# Revit family: LAMP_HANCE TRACK FLOOD (DALI)
name_source: partatom
category: Modelos genéricos
revit_build: Autodesk Revit 2015 (Build: 20140606_1530(x64)
units: mm (PartAtom-declared; Revit-internal decimal feet)

## types (16) — shared parameters
CRI = 80
Comentarios de tipo = Availability of tilting between 0º and 90º, rotation between 0º and 355º and change ring color when placed in a project.
Elevación por defecto = 1219 mm
Fabricante = LAMP
Gear = Adjustable DALI
Installation instructions = http://www.lamp.es
Insulation class = I
Lamp = COB LED
Last update = 08/08/2018
Luminaire type = Indoor - Spotlight
MacAdam = 3
Manufacturer URL = http://www.lamp.es
Manufacturer country = Spain
Manufacturer name = LAMP
Model explanation = Availability of tilting between 0º and 90º, rotation between 0º and 355º and change ring color when placed in a project.
Power Supply = 220-240V 50-60Hz
Product URL = http://www.lamp.es
Product datasheet = http://www.lamp.es
Protection rating = IP20
Type = COB PHILIPS

## per-type parameters (varying)
| type | Altura tija | Anchura tija | Body height | Descripción | Diameter | Efficacy | Finish | IEE | Initial color | Initial intensity | LED Lifetime | Longitud aro | Longitud cuerpo | Material tija | Material track | Modelo | Photometric web file | Plum | Power | Product code | Profundidad tija | Total height | Weight |
| 639LM 3000 BLACK | 63 mm  [stored 0.206693 ft] | 23 mm  [stored 0.0754593 ft] | 135 mm  [stored 0.442913 ft] | HANCE TRACK 220 1000 WW FL BK. | 65 mm  [stored 0.213255 ft] | 78 lm/W | Texturised black | A+ | 3000 K | 639 lm | 50.000 L90 B10 | 64 mm | 135 mm  [stored 0.442913 ft] | LAMP_Aluminio Hance Negro | LAMP_Aluminio Hance Negro | HS1TK10FL830DBB | Cuerpo Hance TRACK FLOOD (tilting) : 639LM 3000 BLACK | 8 W | 7 W | HS1TK10FL830DBB | 8 mm  [stored 0.0262467 ft] | 190 mm | 0.47 kg |
| 639LM 3000 WHITE | 63 mm  [stored 0.206693 ft] | 23 mm  [stored 0.0754593 ft] | 135 mm  [stored 0.442913 ft] | HANCE TRACK 220 1000 WW FL WH. | 65 mm  [stored 0.213255 ft] | 78 lm/W | Texturised matt white | A+ | 3000 K | 639 lm | 50.000 L90 B10 | 64 mm | 135 mm  [stored 0.442913 ft] | LAMP_Aluminio Hance Blanco | LAMP_Aluminio Hance Blanco | HS1TK10FL830DBW | Cuerpo Hance TRACK FLOOD (tilting) : 639LM 3000 WHITE | 8 W | 7 W | HS1TK10FL830DBW | 8 mm  [stored 0.0262467 ft] | 190 mm | 0.47 kg |
| 675LM 4000 BLACK | 63 mm  [stored 0.206693 ft] | 23 mm  [stored 0.0754593 ft] | 135 mm  [stored 0.442913 ft] | HANCE TRACK 220 1000 NW FL BK. | 65 mm  [stored 0.213255 ft] | 82 lm/W | Texturised black | A+ | 4000 K | 675 lm | 50.000 L90 B10 | 64 mm | 135 mm  [stored 0.442913 ft] | LAMP_Aluminio Hance Negro | LAMP_Aluminio Hance Negro | HS1TK10FL840DBB | Cuerpo Hance TRACK FLOOD (tilting) : 675LM 4000 BLACK | 8 W | 7 W | HS1TK10FL840DBB | 8 mm  [stored 0.0262467 ft] | 190 mm | 0.47 kg |
| 675LM 4000 WHITE | 63 mm  [stored 0.206693 ft] | 23 mm  [stored 0.0754593 ft] | 135 mm  [stored 0.442913 ft] | HANCE TRACK 220 1000 NW FL WH. | 65 mm  [stored 0.213255 ft] | 82 lm/W | Texturised matt white | A+ | 4000 K | 675 lm | 50.000 L90 B10 | 64 mm | 135 mm  [stored 0.442913 ft] | LAMP_Aluminio Hance Blanco | LAMP_Aluminio Hance Blanco | HS1TK10FL840DBW | Cuerpo Hance TRACK FLOOD (tilting) : 675LM 4000 WHITE | 8 W | 7 W | HS1TK10FL840DBW | 8 mm  [stored 0.0262467 ft] | 190 mm | 0.47 kg |
| 1476LM 3000 BLACK | 63 mm  [stored 0.206693 ft] | 23 mm  [stored 0.0754593 ft] | 170 mm  [stored 0.557743 ft] | HANCE TRACK 220 2000 WW FL BK. | 65 mm  [stored 0.213255 ft] | 70 lm/W | Texturised black | A | 3000 K | 1476 lm | 50.000 L80 B10 | 99 mm | 170 mm  [stored 0.557743 ft] | LAMP_Aluminio Hance Negro | LAMP_Aluminio Hance Negro | HS1TK20FL830DBB | Cuerpo Hance TRACK FLOOD (tilting) : 1476LM 3000 BLACK | 21 W | 18 W | HS1TK20FL830DBB | 8 mm  [stored 0.0262467 ft] | 225 mm  [stored 0.738189 ft] | 0.65 kg |
| 1476LM 3000 WHITE | 63 mm  [stored 0.206693 ft] | 23 mm  [stored 0.0754593 ft] | 170 mm  [stored 0.557743 ft] | HANCE TRACK 220 2000 WW FL WH. | 65 mm  [stored 0.213255 ft] | 70 lm/W | Texturised matt white | A | 3000 K | 1476 lm | 50.000 L80 B10 | 99 mm | 170 mm  [stored 0.557743 ft] | LAMP_Aluminio Hance Blanco | LAMP_Aluminio Hance Blanco | HS1TK20FL830DBW | Cuerpo Hance TRACK FLOOD (tilting) : 1476LM 3000 WHITE | 21 W | 18 W | HS1TK20FL830DBW | 8 mm  [stored 0.0262467 ft] | 225 mm  [stored 0.738189 ft] | 0.65 kg |
| 1560LM 4000 BLACK | 63 mm  [stored 0.206693 ft] | 23 mm  [stored 0.0754593 ft] | 170 mm  [stored 0.557743 ft] | HANCE TRACK 220 2000 NW FL BK. | 65 mm  [stored 0.213255 ft] | 74 lm/W | Texturised black | A | 4000 K | 1560 lm | 50.000 L80 B10 | 99 mm | 170 mm  [stored 0.557743 ft] | LAMP_Aluminio Hance Negro | LAMP_Aluminio Hance Negro | HS1TK20FL840DBB
HS1TK20FL840NBB | Cuerpo Hance TRACK FLOOD (tilting) : 1560LM 4000 BLACK | 21 W | 18 W | HS1TK20FL840DBB
HS1TK20FL840NBB | 8 mm  [stored 0.0262467 ft] | 225 mm  [stored 0.738189 ft] | 0.65 kg |
| 1560LM 4000 WHITE | 63 mm  [stored 0.206693 ft] | 23 mm  [stored 0.0754593 ft] | 170 mm  [stored 0.557743 ft] | HANCE TRACK 220 2000 NW FL WH. | 65 mm  [stored 0.213255 ft] | 74 lm/W | Texturised matt white | A | 4000 K | 1560 lm | 50.000 L80 B10 | 99 mm | 170 mm  [stored 0.557743 ft] | LAMP_Aluminio Hance Blanco | LAMP_Aluminio Hance Blanco | HS1TK20FL840DBW
HS1TK20FL840NBB | Cuerpo Hance TRACK FLOOD (tilting) : 1560LM 4000 WHITE | 21 W | 18 W | HS1TK20FL840DBW
HS1TK20FL840NBB | 8 mm  [stored 0.0262467 ft] | 225 mm  [stored 0.738189 ft] | 0.65 kg |
| 2569LM 3000 BLACK | 49 mm  [stored 0.160761 ft] | 28 mm  [stored 0.0918635 ft] | 210 mm  [stored 0.688976 ft] | HANCE TRACK 220 3000 WW FL BK. | 90 mm  [stored 0.295276 ft] | 90 lm/W | Texturised black | A+ | 3000 K | 2569 lm | 50.000 L80 B10 | 139 mm | 210 mm  [stored 0.688976 ft] | LAMP_Aluminio Hance Negro | LAMP_Aluminio Hance Negro | HS1TK30FL830DBB | Cuerpo Hance TRACK FLOOD (tilting) : 2569LM 3000 BLACK | 29 W | 26 W | HS1TK30FL830DBB | 18 mm  [stored 0.0590551 ft] | 266 mm  [stored 0.872703 ft] | 1.35 kg |
| 2569LM 3000 WHITE | 49 mm  [stored 0.160761 ft] | 28 mm  [stored 0.0918635 ft] | 210 mm  [stored 0.688976 ft] | HANCE TRACK 220 3000 WW FL WH. | 90 mm  [stored 0.295276 ft] | 90 lm/W | Texturised matt white | A+ | 3000 K | 2569 lm | 50.000 L80 B10 | 139 mm | 210 mm  [stored 0.688976 ft] | LAMP_Aluminio Hance Blanco | LAMP_Aluminio Hance Blanco | HS1TK30FL830DBW | Cuerpo Hance TRACK FLOOD (tilting) : 2569LM 3000 WHITE | 29 W | 26 W | HS1TK30FL830DBW | 18 mm  [stored 0.0590551 ft] | 266 mm  [stored 0.872703 ft] | 1.35 kg |
| 2686LM 4000 BLACK | 49 mm  [stored 0.160761 ft] | 28 mm  [stored 0.0918635 ft] | 210 mm  [stored 0.688976 ft] | HANCE TRACK 220 3000 NW FL BK. | 90 mm  [stored 0.295276 ft] | 94 lm/W | Texturised black | A+ | 4000 K | 2686 lm | 50.000 L80 B10 | 139 mm | 210 mm  [stored 0.688976 ft] | LAMP_Aluminio Hance Negro | LAMP_Aluminio Hance Negro | HS1TK30FL840DBB | Cuerpo Hance TRACK FLOOD (tilting) : 2686LM 4000 BLACK | 29 W | 26 W | HS1TK30FL840DBB | 18 mm  [stored 0.0590551 ft] | 266 mm  [stored 0.872703 ft] | 1.35 kg |
| 2686LM 4000 WHITE | 49 mm  [stored 0.160761 ft] | 28 mm  [stored 0.0918635 ft] | 210 mm  [stored 0.688976 ft] | HANCE TRACK 220 3000 NW FL WH. | 90 mm  [stored 0.295276 ft] | 94 lm/W | Texturised matt white | A+ | 4000 K | 2686 lm | 50.000 L80 B10 | 139 mm | 210 mm  [stored 0.688976 ft] | LAMP_Aluminio Hance Blanco | LAMP_Aluminio Hance Blanco | HS1TK30FL840DBW | Cuerpo Hance TRACK FLOOD (tilting) : 2686LM 4000 WHITE | 29 W | 26 W | HS1TK30FL840DBW | 18 mm  [stored 0.0590551 ft] | 266 mm  [stored 0.872703 ft] | 1.35 kg |
| 3290LM 3000 BLACK | 49 mm  [stored 0.160761 ft] | 28 mm  [stored 0.0918635 ft] | 210 mm  [stored 0.688976 ft] | HANCE TRACK 220 4000 WW FL BK. | 90 mm  [stored 0.295276 ft] | 83 lm/W | Texturised black | A+ | 3000 K | 3290 lm | 50.000 L80 B10 | 139 mm | 210 mm  [stored 0.688976 ft] | LAMP_Aluminio Hance Negro | LAMP_Aluminio Hance Negro | HS1TK40FL830DBB | Cuerpo Hance TRACK FLOOD (tilting) : 3290LM 3000 BLACK | 40 W | 35 W | HS1TK40FL830DBB | 18 mm  [stored 0.0590551 ft] | 266 mm  [stored 0.872703 ft] | 1.35 kg |
| 3290LM 3000 WHITE | 49 mm  [stored 0.160761 ft] | 28 mm  [stored 0.0918635 ft] | 210 mm  [stored 0.688976 ft] | HANCE TRACK 220 4000 WW FL WH. | 90 mm  [stored 0.295276 ft] | 83 lm/W | Texturised matt white | A+ | 3000 K | 3290 lm | 50.000 L80 B10 | 139 mm | 210 mm  [stored 0.688976 ft] | LAMP_Aluminio Hance Blanco | LAMP_Aluminio Hance Blanco | HS1TK40FL830DBW | Cuerpo Hance TRACK FLOOD (tilting) : 3290LM 3000 WHITE | 40 W | 35 W | HS1TK40FL830DBW | 18 mm  [stored 0.0590551 ft] | 266 mm  [stored 0.872703 ft] | 1.35 kg |
| 3426LM 4000 BLACK | 49 mm  [stored 0.160761 ft] | 28 mm  [stored 0.0918635 ft] | 210 mm  [stored 0.688976 ft] | HANCE TRACK 220 4000 NW FL BK. | 90 mm  [stored 0.295276 ft] | 87 lm/W | Texturised black | A+ | 4000 K | 3426 lm | 50.000 L80 B10 | 139 mm | 210 mm  [stored 0.688976 ft] | LAMP_Aluminio Hance Negro | LAMP_Aluminio Hance Negro | HS1TK40FL840DBB | Cuerpo Hance TRACK FLOOD (tilting) : 3426LM 4000 BLACK | 40 W | 35 W | HS1TK40FL840DBB | 18 mm  [stored 0.0590551 ft] | 266 mm  [stored 0.872703 ft] | 1.35 kg |
| 3426LM 4000 WHITE | 49 mm  [stored 0.160761 ft] | 28 mm  [stored 0.0918635 ft] | 210 mm  [stored 0.688976 ft] | HANCE TRACK 220 4000 NW FL WH. | 90 mm  [stored 0.295276 ft] | 87 lm/W | Texturised matt white | A+ | 4000 K | 3426 lm | 50.000 L80 B10 | 139 mm | 210 mm  [stored 0.688976 ft] | LAMP_Aluminio Hance Blanco | LAMP_Aluminio Hance Blanco | HS1TK40FL840DBW | Cuerpo Hance TRACK FLOOD (tilting) : 3426LM 4000 WHITE | 40 W | 35 W | HS1TK40FL840DBW | 18 mm  [stored 0.0590551 ft] | 266 mm  [stored 0.872703 ft] | 1.35 kg |

note: [stored X ft] marks values corroborated as IEEE doubles in the binary element streams (Revit-internal decimal feet)
